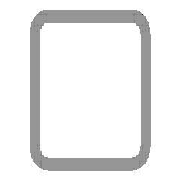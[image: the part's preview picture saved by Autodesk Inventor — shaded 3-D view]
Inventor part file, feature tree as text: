
AUTODESK INVENTOR PART (.ipt)
format: ipt  version: 2022.1 (Build 261234000, 234)  size: 425,472 bytes
history: native  units: mm (DEFAULTED — no unit token found)
features: other x5, plane x5, sketch x4, boolean_combine x2, surface_op x2, split x1, extrude x1
ambient origin geometry x8: Origin, YZ Plane, XZ Plane, XY Plane, X Axis, Y Axis, Z Axis, Center Point
bodies: Solid1 (feature_tree), Body (feature_tree), Solid2 (feature_tree), Solid7 (feature_tree)
feature tree (20):
  parser-record x1  (decoder bookkeeping rows leaked as tree rows — omitted from the tree; the rows remain in map.json)
  other  "Driven Length"
  other  "Start Plane"
  other  "End Plane"
  plane  "Work Plane4"
  split  "Split1"
  plane  "Work Plane5"
  plane  "Work Plane6"
  plane  "Work Plane7"
  extrude  "Extrusion2"  TaperAngle=0.0deg  [1 undecoded]
  boolean_combine  "Combine1"
  surface_op  "Sculpt1"
  boolean_combine  "Combine2"
  sketch  "Sketch"  dims[d11=40.0mm d12=2.0mm d13=-5.182521mm d14=200.730082mm d15=20.0mm d16=20.0mm d17=90.0deg d18=205.912603mm d19=0.12mm d20=0.0mm]
  sketch  "Sketch3"  dims[d3=205.912603mm d4=0.0mm]
  plane  "Work Plane3"
  sketch  "Sketch4"  dims[d7=4.0mm]
  sketch  "Sketch5"  dims[d9=40.0mm]
  surface_op  "Surface1"
  other  "Srf13"
note: 1 required parameter value undecoded (feature->parameter linkage not recoverable at this tier; creation-order binding heuristic only, values carry confidence <= 0.55)
